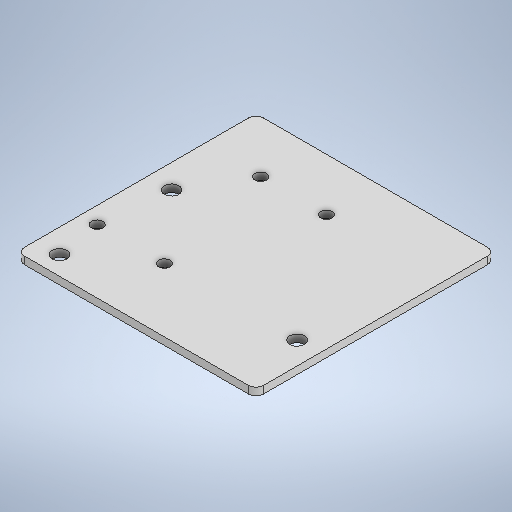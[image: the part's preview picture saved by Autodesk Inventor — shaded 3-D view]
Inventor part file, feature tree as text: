
AUTODESK INVENTOR PART (.ipt)
format: ipt  version: 2025.1 (Build 291241000, 241)  size: 249,856 bytes
history: native  units: in
note: dims shown in document units (in); Inventor stores cm internally (conversion verified against a paired STEP export)
features: extrude x1, fillet x1, sketch x1
ambient origin geometry x8: Origin, YZ Plane, XZ Plane, XY Plane, X Axis, Y Axis, Z Axis, Center Point
bodies: Solid1 (feature_tree)
feature tree (3):
  extrude  "Extrusion1"  Depth=8.0in
  fillet  "Fillet1"  Radius=0.5in
  sketch  "Sketch1"  dims[d0=8.0in d1=8.0in d2=0.5in d3=0.625in d4=0.8in d6=3.75in d7=0.5in d8=0.75in d9=2.125in d10=0.39in d11=1.75in d12=2.2in d13=0.39in d14=0.39in d15=0.56in d16=0.39in d17=2.25in d18=0.25in d19=0.0in d20=0.25in]
